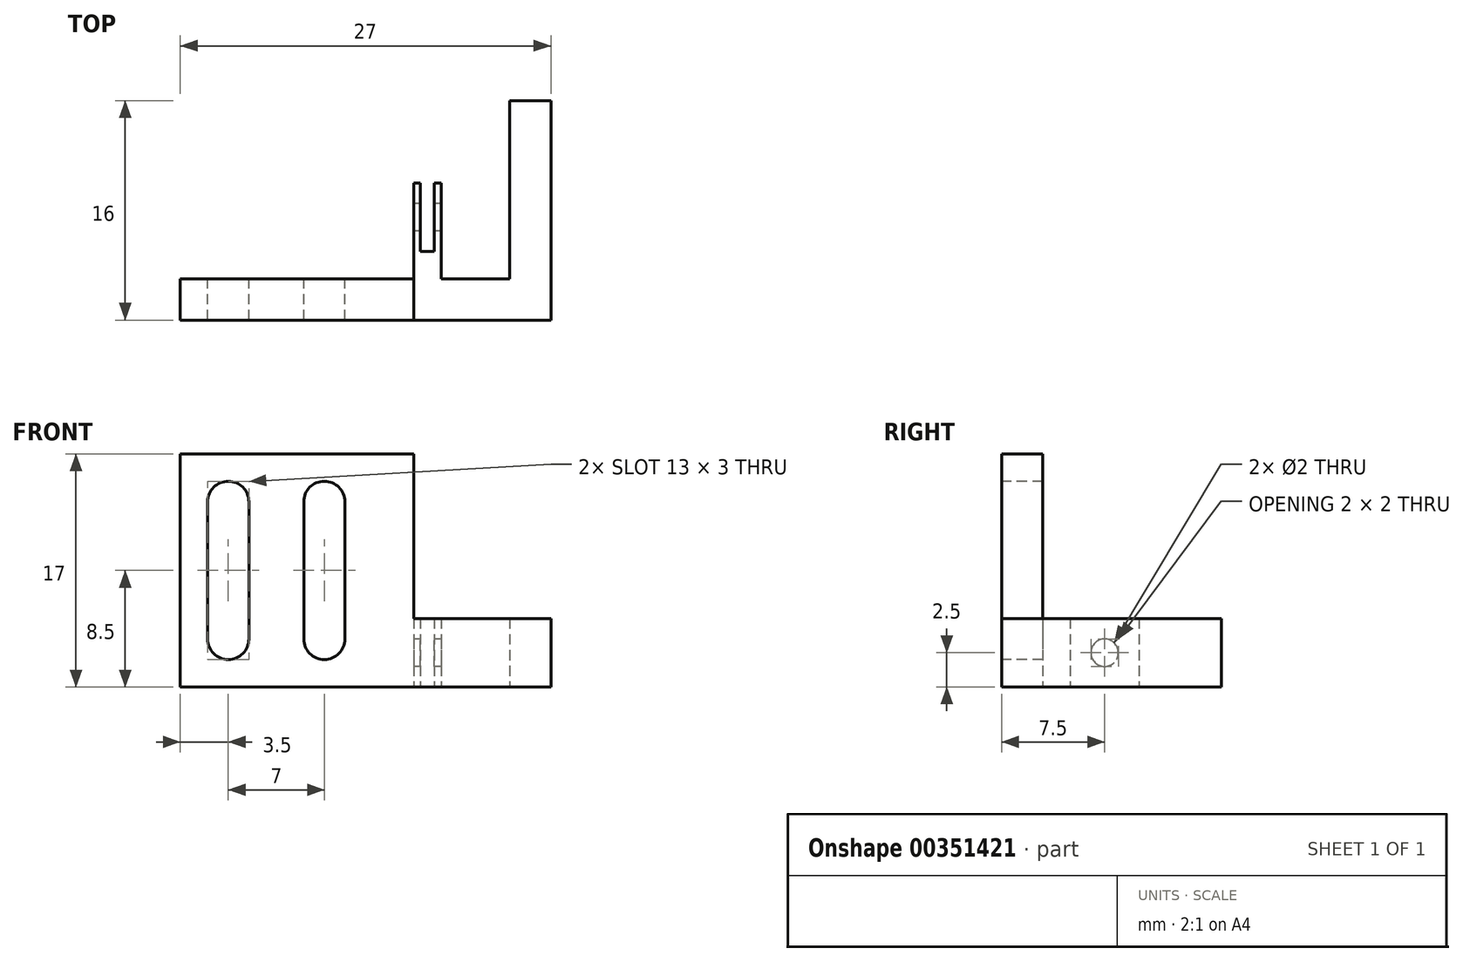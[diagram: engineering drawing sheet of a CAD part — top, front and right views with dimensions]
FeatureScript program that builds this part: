
annotation { "Feature Type Name" : "Feature", "Feature Type Description" : "" }
export const myFeature = defineFeature(function(context is Context, id is Id, definition is map)
    precondition{}
    {
        {
            var Q0;
            Q0=qCreatedBy(makeId("Front.planeOp"),FACE);
            var sketch = newSketch(context, id + "F0", { "sketchPlane" : qUnion([Q0])});
            skLineSegment(sketch, "E0.bottom", {"start": v(8.5, 8.5) * mm, "end": v(-8.5, 8.5) * mm});
            skLineSegment(sketch, "E0.top", {"start": v(8.5, -8.5) * mm, "end": v(-8.5, -8.5) * mm});
            skLineSegment(sketch, "E0.left", {"start": v(8.5, 8.5) * mm, "end": v(8.5, -8.5) * mm});
            skLineSegment(sketch, "E0.right", {"start": v(-8.5, 8.5) * mm, "end": v(-8.5, -8.5) * mm});
            skPoint(sketch, "E0.middle", {"position": v(0, 0) * mm});
            skLineSegment(sketch, "E1.bottom", {"start": v(-3.5, 6.5) * mm, "end": v(-6.5, 6.5) * mm});
            skLineSegment(sketch, "E1.top", {"start": v(-3.5, -6.5) * mm, "end": v(-6.5, -6.5) * mm});
            skLineSegment(sketch, "E1.left", {"start": v(-3.5, 6.5) * mm, "end": v(-3.5, -6.5) * mm});
            skLineSegment(sketch, "E1.right", {"start": v(-6.5, 6.5) * mm, "end": v(-6.5, -6.5) * mm});
            skPoint(sketch, "E1.middle", {"position": v(-5, 0) * mm});
            skLineSegment(sketch, "E2.bottom", {"start": v(3.5, 6.5) * mm, "end": v(0.5, 6.5) * mm});
            skLineSegment(sketch, "E2.top", {"start": v(3.5, -6.5) * mm, "end": v(0.5, -6.5) * mm});
            skLineSegment(sketch, "E2.left", {"start": v(3.5, 6.5) * mm, "end": v(3.5, -6.5) * mm});
            skLineSegment(sketch, "E2.right", {"start": v(0.5, 6.5) * mm, "end": v(0.5, -6.5) * mm});
            skPoint(sketch, "E2.middle", {"position": v(2, 0) * mm});
            skSolve(sketch);
        }
        {
            var Q0;
            Q0=qSketchRegion(id+"F0",true);
            extrude(context, id + "F1", {"entities" : qUnion([Q0]), "depth" : 3 * mm});
        }
        {
            var Q0;
            Q0=makeQuery(id+"F1.opExtrude","SWEPT_FACE",FACE,{"disambiguationData":[OSD([sQuery(id+"F0.wireOp",EDGE,"E0.left")])]});
            var sketch = newSketch(context, id + "F2", { "sketchPlane" : qUnion([Q0])});
            skLineSegment(sketch, "E3.bottom", {"start": v(-3, -3.5) * mm, "end": v(0, -3.5) * mm});
            skLineSegment(sketch, "E3.top", {"start": v(-3, -8.5) * mm, "end": v(0, -8.5) * mm});
            skLineSegment(sketch, "E3.left", {"start": v(-3, -3.5) * mm, "end": v(-3, -8.5) * mm});
            skLineSegment(sketch, "E3.right", {"start": v(0, -3.5) * mm, "end": v(0, -8.5) * mm});
            skSolve(sketch);
        }
        {
            var Q0;
            Q0=qSketchRegion(id+"F2",true);
            extrude(context, id + "F3", {"entities" : qUnion([Q0]), "operationType" : NewBodyOperationType.ADD, "depth" : 10 * mm});
        }
        {
            var Q0;
            Q0=makeQuery(id+"F3.boolean.opBoolean","MERGE",FACE,{"derivedFrom":[makeQuery(id+"F1.opExtrude","CAP_FACE",FACE,{"disambiguationData":[OSD([sQuery(id+"F0.wireOp",EDGE,"E0.bottom"),sQuery(id+"F0.wireOp",EDGE,"E0.top"),sQuery(id+"F0.wireOp",EDGE,"E0.left"),sQuery(id+"F0.wireOp",EDGE,"E0.right"),sQuery(id+"F0.wireOp",EDGE,"E1.bottom"),sQuery(id+"F0.wireOp",EDGE,"E1.top"),sQuery(id+"F0.wireOp",EDGE,"E1.left"),sQuery(id+"F0.wireOp",EDGE,"E1.right"),sQuery(id+"F0.wireOp",EDGE,"E2.bottom"),sQuery(id+"F0.wireOp",EDGE,"E2.top"),sQuery(id+"F0.wireOp",EDGE,"E2.left"),sQuery(id+"F0.wireOp",EDGE,"E2.right")])],"isStart":true}),makeQuery(id+"F3.opExtrude","SWEPT_FACE",FACE,{"disambiguationData":[OSD([sQuery(id+"F2.wireOp",EDGE,"E3.right")])]})]});
            var sketch = newSketch(context, id + "F4", { "sketchPlane" : qUnion([Q0])});
            skLineSegment(sketch, "E4.bottom", {"start": v(-18.5, -3.5) * mm, "end": v(-15.5, -3.5) * mm});
            skLineSegment(sketch, "E4.top", {"start": v(-18.5, -8.5) * mm, "end": v(-15.5, -8.5) * mm});
            skLineSegment(sketch, "E4.left", {"start": v(-18.5, -3.5) * mm, "end": v(-18.5, -8.5) * mm});
            skLineSegment(sketch, "E4.right", {"start": v(-15.5, -3.5) * mm, "end": v(-15.5, -8.5) * mm});
            skSolve(sketch);
        }
        {
            var Q0;
            Q0=qSketchRegion(id+"F4",true);
            extrude(context, id + "F5", {"entities" : qUnion([Q0]), "operationType" : NewBodyOperationType.ADD, "depth" : 13 * mm});
        }
        {
            var Q0;
            Q0=makeQuery(id+"F3.boolean.opBoolean","MERGE",FACE,{"derivedFrom":[makeQuery(id+"F1.opExtrude","CAP_FACE",FACE,{"disambiguationData":[OSD([sQuery(id+"F0.wireOp",EDGE,"E0.bottom"),sQuery(id+"F0.wireOp",EDGE,"E0.top"),sQuery(id+"F0.wireOp",EDGE,"E0.left"),sQuery(id+"F0.wireOp",EDGE,"E0.right"),sQuery(id+"F0.wireOp",EDGE,"E1.bottom"),sQuery(id+"F0.wireOp",EDGE,"E1.top"),sQuery(id+"F0.wireOp",EDGE,"E1.left"),sQuery(id+"F0.wireOp",EDGE,"E1.right"),sQuery(id+"F0.wireOp",EDGE,"E2.bottom"),sQuery(id+"F0.wireOp",EDGE,"E2.top"),sQuery(id+"F0.wireOp",EDGE,"E2.left"),sQuery(id+"F0.wireOp",EDGE,"E2.right")])],"isStart":true}),makeQuery(id+"F3.opExtrude","SWEPT_FACE",FACE,{"disambiguationData":[OSD([sQuery(id+"F2.wireOp",EDGE,"E3.right")])]})]});
            var sketch = newSketch(context, id + "F6", { "sketchPlane" : qUnion([Q0])});
            skLineSegment(sketch, "E5.bottom", {"start": v(-8.5, -3.5) * mm, "end": v(-10.5, -3.5) * mm});
            skLineSegment(sketch, "E5.top", {"start": v(-8.5, -8.5) * mm, "end": v(-10.5, -8.5) * mm});
            skLineSegment(sketch, "E5.left", {"start": v(-8.5, -3.5) * mm, "end": v(-8.5, -8.5) * mm});
            skLineSegment(sketch, "E5.right", {"start": v(-10.5, -3.5) * mm, "end": v(-10.5, -8.5) * mm});
            skSolve(sketch);
        }
        {
            var Q0;
            Q0=qSketchRegion(id+"F6",true);
            extrude(context, id + "F7", {"entities" : qUnion([Q0]), "operationType" : NewBodyOperationType.ADD, "depth" : 7 * mm});
        }
        {
            var Q0;
            Q0=makeQuery(id+"F7.opExtrude","CAP_FACE",FACE,{"disambiguationData":[OSD([sQuery(id+"F6.wireOp",EDGE,"E5.bottom"),sQuery(id+"F6.wireOp",EDGE,"E5.top"),sQuery(id+"F6.wireOp",EDGE,"E5.left"),sQuery(id+"F6.wireOp",EDGE,"E5.right")])],"isStart":false});
            var sketch = newSketch(context, id + "F8", { "sketchPlane" : qUnion([Q0])});
            skLineSegment(sketch, "E6.bottom", {"start": v(-10, -3.5) * mm, "end": v(-9, -3.5) * mm});
            skLineSegment(sketch, "E6.top", {"start": v(-10, -8.5) * mm, "end": v(-9, -8.5) * mm});
            skLineSegment(sketch, "E6.left", {"start": v(-10, -3.5) * mm, "end": v(-10, -8.5) * mm});
            skLineSegment(sketch, "E6.right", {"start": v(-9, -3.5) * mm, "end": v(-9, -8.5) * mm});
            skSolve(sketch);
        }
        {
            var Q0;
            Q0=qSketchRegion(id+"F8",true);
            extrude(context, id + "F9", {"entities" : qUnion([Q0]), "operationType" : NewBodyOperationType.REMOVE, "oppositeDirection" : true, "depth" : 5 * mm});
        }
        {
            var Q0;
            Q0=makeQuery(id+"F7.opExtrude","SWEPT_FACE",FACE,{"disambiguationData":[OSD([sQuery(id+"F6.wireOp",EDGE,"E5.left")])]});
            var sketch = newSketch(context, id + "F10", { "sketchPlane" : qUnion([Q0])});
            skCircle(sketch, "E7", {"center": v(-4.5, -6) * mm, "radius": 1 * mm});
            skPoint(sketch, "E7.centerSnap0", {"position": v(-7, -6) * mm});
            skSolve(sketch);
        }
        {
            var Q0;
            Q0=qSketchRegion(id+"F10",true);
            extrude(context, id + "F11", {"entities" : qUnion([Q0]), "operationType" : NewBodyOperationType.REMOVE, "oppositeDirection" : true, "depth" : 3 * mm});
        }
        {
            var Q0;
            Q0=makeQuery(id+"F1.opExtrude","SWEPT_EDGE",EDGE,{"disambiguationData":[OSD([sQuery(id+"F0.wireOp",EDGE,"E1.bottom"),sQuery(id+"F0.wireOp",EDGE,"E1.right")])]});
            var Q1;
            Q1=makeQuery(id+"F1.opExtrude","SWEPT_EDGE",EDGE,{"disambiguationData":[OSD([sQuery(id+"F0.wireOp",EDGE,"E2.bottom"),sQuery(id+"F0.wireOp",EDGE,"E2.right")])]});
            var Q2;
            Q2=makeQuery(id+"F1.opExtrude","SWEPT_EDGE",EDGE,{"disambiguationData":[OSD([sQuery(id+"F0.wireOp",EDGE,"E2.bottom"),sQuery(id+"F0.wireOp",EDGE,"E2.left")])]});
            var Q3;
            Q3=makeQuery(id+"F1.opExtrude","SWEPT_EDGE",EDGE,{"disambiguationData":[OSD([sQuery(id+"F0.wireOp",EDGE,"E1.bottom"),sQuery(id+"F0.wireOp",EDGE,"E1.left")])]});
            var Q4;
            Q4=makeQuery(id+"F1.opExtrude","SWEPT_EDGE",EDGE,{"disambiguationData":[OSD([sQuery(id+"F0.wireOp",EDGE,"E1.top"),sQuery(id+"F0.wireOp",EDGE,"E1.left")])]});
            var Q5;
            Q5=makeQuery(id+"F1.opExtrude","SWEPT_EDGE",EDGE,{"disambiguationData":[OSD([sQuery(id+"F0.wireOp",EDGE,"E2.top"),sQuery(id+"F0.wireOp",EDGE,"E2.left")])]});
            var Q6;
            Q6=makeQuery(id+"F1.opExtrude","SWEPT_EDGE",EDGE,{"disambiguationData":[OSD([sQuery(id+"F0.wireOp",EDGE,"E2.top"),sQuery(id+"F0.wireOp",EDGE,"E2.right")])]});
            var Q7;
            Q7=makeQuery(id+"F1.opExtrude","SWEPT_EDGE",EDGE,{"disambiguationData":[OSD([sQuery(id+"F0.wireOp",EDGE,"E1.top"),sQuery(id+"F0.wireOp",EDGE,"E1.right")])]});
            fillet(context, id + "F12", {"entities" : qUnion([Q0, Q1, Q2, Q3, Q4, Q5, Q6, Q7]), "radius" : 1.5 * mm, "tangentPropagation" : true, "allowEdgeOverflow" : false});
        }
    });
